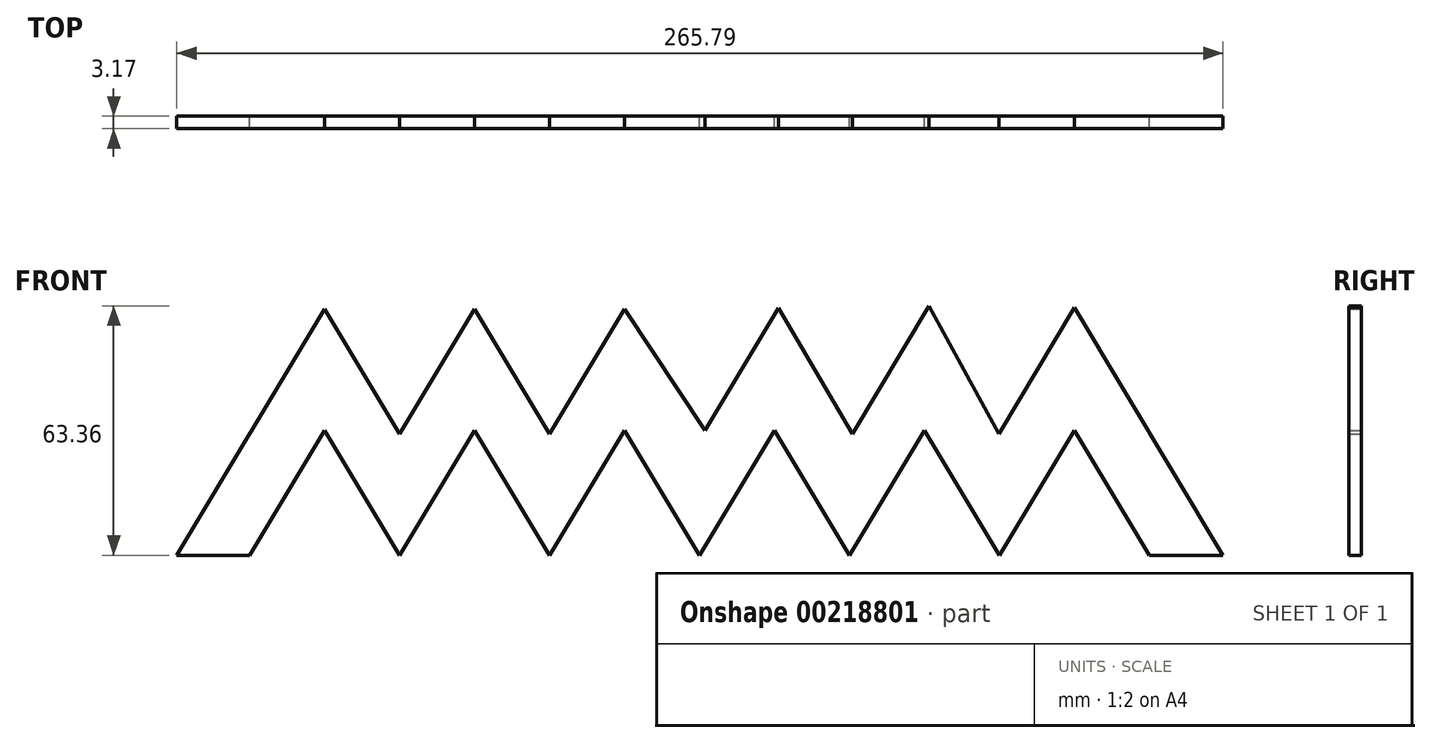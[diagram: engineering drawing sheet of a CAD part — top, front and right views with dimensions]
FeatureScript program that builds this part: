
annotation { "Feature Type Name" : "Feature", "Feature Type Description" : "" }
export const myFeature = defineFeature(function(context is Context, id is Id, definition is map)
    precondition{}
    {
        {
            var Q0;
            Q0=qCreatedBy(makeId("Front.planeOp"),FACE);
            var sketch = newSketch(context, id + "F0", { "sketchPlane" : qUnion([Q0])});
            skLineSegment(sketch, "E0", {"start": v(-79.24, 31.75) * mm, "end": v(-98.3, 0) * mm});
            skLineSegment(sketch, "E1", {"start": v(-79.24, 31.75) * mm, "end": v(-60.2, 0) * mm});
            skLineSegment(sketch, "E2.1.0.0", {"start": v(-41.14, 31.75) * mm, "end": v(-60.2, 0) * mm});
            skLineSegment(sketch, "E2.1.0.1", {"start": v(-41.14, 31.75) * mm, "end": v(-22.1, 0) * mm});
            skLineSegment(sketch, "E2.2.0.0", {"start": v(-3.04, 31.75) * mm, "end": v(-22.1, 0) * mm});
            skLineSegment(sketch, "E2.2.0.1", {"start": v(-3.04, 31.75) * mm, "end": v(16, 0) * mm});
            skLineSegment(sketch, "E2.3.0.0", {"start": v(35.06, 31.75) * mm, "end": v(16, 0) * mm});
            skLineSegment(sketch, "E2.3.0.1", {"start": v(35.06, 31.75) * mm, "end": v(54.1, 0) * mm});
            skLineSegment(sketch, "E2.4.0.0", {"start": v(73.16, 31.75) * mm, "end": v(54.1, 0) * mm});
            skLineSegment(sketch, "E2.4.0.1", {"start": v(73.16, 31.75) * mm, "end": v(92.2, 0) * mm});
            skLineSegment(sketch, "E2.5.0.0", {"start": v(111.26, 31.75) * mm, "end": v(92.2, 0) * mm});
            skLineSegment(sketch, "E2.5.0.1", {"start": v(111.26, 31.75) * mm, "end": v(130.3, 0) * mm});
            skLineSegment(sketch, "E2.direction1", {"start": v(-98.3, 0) * mm, "end": v(-60.2, 0) * mm, "construction": true});
            skLineSegment(sketch, "E3", {"start": v(-116.8, 0) * mm, "end": v(-79.24, 62.6) * mm});
            skLineSegment(sketch, "E4", {"start": v(-79.24, 62.6) * mm, "end": v(-60.2, 30.86) * mm});
            skLineSegment(sketch, "E5", {"start": v(-60.2, 30.86) * mm, "end": v(-41.14, 62.6) * mm});
            skLineSegment(sketch, "E6", {"start": v(-41.14, 62.6) * mm, "end": v(-22.1, 30.86) * mm});
            skLineSegment(sketch, "E7", {"start": v(-22.1, 30.86) * mm, "end": v(-3.04, 62.6) * mm});
            skLineSegment(sketch, "E8", {"start": v(-3.04, 62.6) * mm, "end": v(17.43, 31.75) * mm});
            skLineSegment(sketch, "E9", {"start": v(17.43, 31.75) * mm, "end": v(36.04, 62.78) * mm});
            skLineSegment(sketch, "E10", {"start": v(36.04, 62.78) * mm, "end": v(54.8, 30.86) * mm});
            skLineSegment(sketch, "E11", {"start": v(54.8, 30.86) * mm, "end": v(74.3, 63.36) * mm});
            skLineSegment(sketch, "E12", {"start": v(74.3, 63.36) * mm, "end": v(92.04, 30.86) * mm});
            skLineSegment(sketch, "E13", {"start": v(92.04, 30.86) * mm, "end": v(111.26, 62.9) * mm});
            skLineSegment(sketch, "E14", {"start": v(111.26, 62.9) * mm, "end": v(149, 0) * mm});
            skLineSegment(sketch, "E15", {"start": v(-116.8, 0) * mm, "end": v(-98.3, 0) * mm});
            skLineSegment(sketch, "E16", {"start": v(130.3, 0) * mm, "end": v(149, 0) * mm});
            skSolve(sketch);
        }
        {
            var Q0;
            Q0 = qSketchRegion(id + "F0", true);
            extrude(context, id + "F1", {"entities" : qUnion([Q0]), "depth" : 3.17 * mm});
        }
    });
